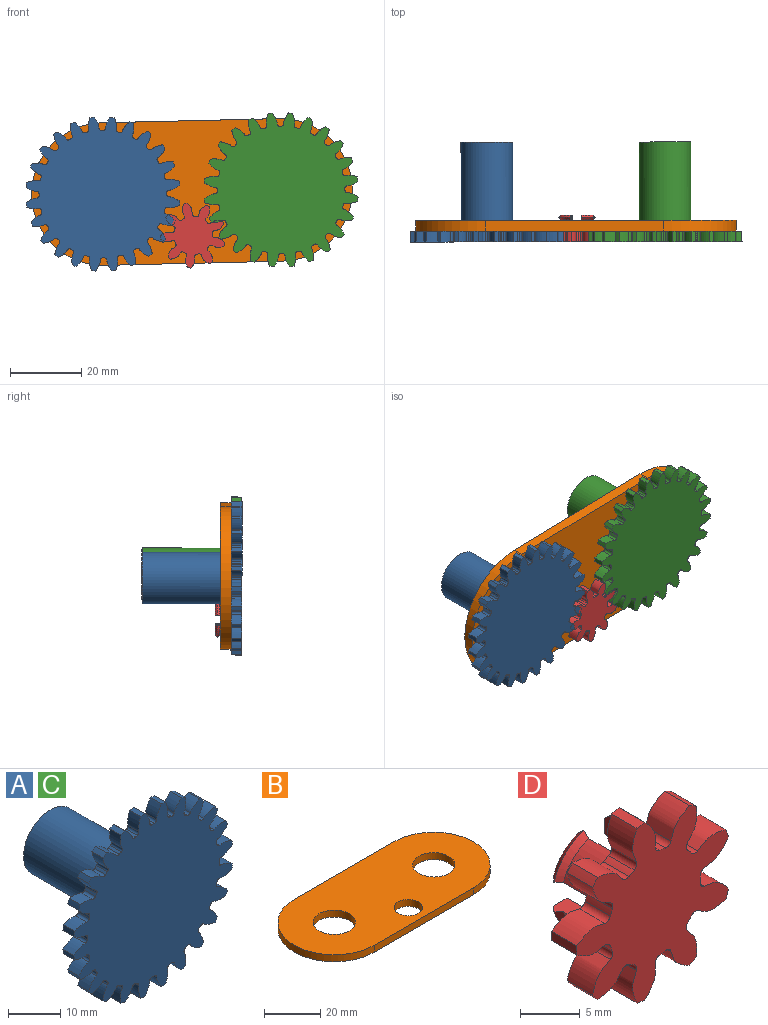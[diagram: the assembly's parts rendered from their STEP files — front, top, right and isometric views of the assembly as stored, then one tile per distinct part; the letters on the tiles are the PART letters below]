
ASSEMBLY  parts=4 mates=6
PART A: 148 faces, bbox 43.1x28x43.1 mm
  f0: extruded ~3.06x3mm, area 10.1mm2, adj f95,f96,f97,f98
  f1: cylinder r=17.92mm len=3mm, axis (0,1,0), area 1.9mm2, adj f96,f97,f98,f99
  f2: extruded ~3.06x3mm, area 10.1mm2, adj f3,f96,f97,f99
  f3: cylinder r=21.67mm len=3mm, axis (0,1,0), area 3.6mm2, adj f2,f4,f96,f97
  f4: extruded ~3.3x3mm, area 10.1mm2, adj f3,f96,f97,f100
  f5: cylinder r=17.92mm len=3mm, axis (0,1,0), area 1.9mm2, adj f96,f97,f100,f101
  f6: extruded ~3x2.62mm, area 10.1mm2, adj f7,f96,f97,f101
  f7: cylinder r=21.67mm len=3mm, axis (0,1,0), area 3.6mm2, adj f6,f8,f96,f97
  f8: extruded ~3.31x3mm, area 10.1mm2, adj f7,f96,f97,f102
  f9: cylinder r=17.92mm len=3mm, axis (0,1,0), area 1.9mm2, adj f96,f97,f102,f103
  f10: extruded ~3x2.66mm, area 10.1mm2, adj f11,f96,f97,f103
  f11: cylinder r=21.67mm len=3mm, axis (0,1,0), area 3.6mm2, adj f10,f12,f96,f97
  f12: extruded ~3.09x3mm, area 10.1mm2, adj f11,f96,f97,f104
  f13: cylinder r=17.92mm len=3mm, axis (0,1,0), area 1.9mm2, adj f96,f97,f104,f105
  f14: extruded ~3.09x3mm, area 10.1mm2, adj f15,f96,f97,f105
  f15: cylinder r=21.67mm len=3mm, axis (0,1,0), area 3.6mm2, adj f14,f16,f96,f97
  f16: extruded ~3x2.66mm, area 10.1mm2, adj f15,f96,f97,f106
  f17: cylinder r=17.92mm len=3mm, axis (0,1,0), area 1.9mm2, adj f96,f97,f106,f107
  f18: extruded ~3.31x3mm, area 10.1mm2, adj f19,f96,f97,f107
  f19: cylinder r=21.67mm len=3mm, axis (0,1,0), area 3.6mm2, adj f18,f20,f96,f97
  f20: extruded ~3x2.62mm, area 10.1mm2, adj f19,f96,f97,f108
  f21: cylinder r=17.92mm len=3mm, axis (0,1,0), area 1.9mm2, adj f96,f97,f108,f109
  f22: extruded ~3.3x3mm, area 10.1mm2, adj f23,f96,f97,f109
  f23: cylinder r=21.67mm len=3mm, axis (0,1,0), area 3.6mm2, adj f22,f24,f96,f97
  f24: extruded ~3.06x3mm, area 10.1mm2, adj f23,f96,f97,f110
  f25: cylinder r=17.92mm len=3mm, axis (0,1,0), area 1.9mm2, adj f96,f97,f110,f111
  f26: extruded ~3.06x3mm, area 10.1mm2, adj f27,f96,f97,f111
  f27: cylinder r=21.67mm len=3mm, axis (0,1,0), area 3.6mm2, adj f26,f28,f96,f97
  f28: extruded ~3.3x3mm, area 10.1mm2, adj f27,f96,f97,f112
  f29: cylinder r=17.92mm len=3mm, axis (0,1,0), area 1.9mm2, adj f96,f97,f112,f113
  f30: extruded ~3x2.62mm, area 10.1mm2, adj f31,f96,f97,f113
  f31: cylinder r=21.67mm len=3mm, axis (0,1,0), area 3.6mm2, adj f30,f32,f96,f97
  f32: extruded ~3.31x3mm, area 10.1mm2, adj f31,f96,f97,f114
  f33: cylinder r=17.92mm len=3mm, axis (0,1,0), area 1.9mm2, adj f96,f97,f114,f115
  f34: extruded ~3x2.66mm, area 10.1mm2, adj f35,f96,f97,f115
  f35: cylinder r=21.67mm len=3mm, axis (0,1,0), area 3.6mm2, adj f34,f36,f96,f97
  f36: extruded ~3.09x3mm, area 10.1mm2, adj f35,f96,f97,f116
  f37: cylinder r=17.92mm len=3mm, axis (0,1,0), area 1.9mm2, adj f96,f97,f116,f117
  f38: extruded ~3.09x3mm, area 10.1mm2, adj f39,f96,f97,f117
  f39: cylinder r=21.67mm len=3mm, axis (0,1,0), area 3.6mm2, adj f38,f40,f96,f97
  f40: extruded ~3x2.66mm, area 10.1mm2, adj f39,f96,f97,f118
  f41: cylinder r=17.92mm len=3mm, axis (0,1,0), area 1.9mm2, adj f96,f97,f118,f119
  f42: extruded ~3.31x3mm, area 10.1mm2, adj f43,f96,f97,f119
  f43: cylinder r=21.67mm len=3mm, axis (0,1,0), area 3.6mm2, adj f42,f44,f96,f97
  f44: extruded ~3x2.62mm, area 10.1mm2, adj f43,f96,f97,f120
  f45: cylinder r=17.92mm len=3mm, axis (0,1,0), area 1.9mm2, adj f96,f97,f120,f121
  f46: extruded ~3.3x3mm, area 10.1mm2, adj f47,f96,f97,f121
  f47: cylinder r=21.67mm len=3mm, axis (0,1,0), area 3.6mm2, adj f46,f48,f96,f97
  f48: extruded ~3.06x3mm, area 10.1mm2, adj f47,f96,f97,f122
  f49: cylinder r=17.92mm len=3mm, axis (0,1,0), area 1.9mm2, adj f96,f97,f122,f123
  f50: extruded ~3.06x3mm, area 10.1mm2, adj f51,f96,f97,f123
  f51: cylinder r=21.67mm len=3mm, axis (0,1,0), area 3.6mm2, adj f50,f52,f96,f97
  f52: extruded ~3.3x3mm, area 10.1mm2, adj f51,f96,f97,f124
  f53: cylinder r=17.92mm len=3mm, axis (0,1,0), area 1.9mm2, adj f96,f97,f124,f125
  f54: extruded ~3x2.62mm, area 10.1mm2, adj f55,f96,f97,f125
  f55: cylinder r=21.67mm len=3mm, axis (0,1,0), area 3.6mm2, adj f54,f56,f96,f97
  f56: extruded ~3.31x3mm, area 10.1mm2, adj f55,f96,f97,f126
  f57: cylinder r=17.92mm len=3mm, axis (0,1,0), area 1.9mm2, adj f96,f97,f126,f127
  f58: extruded ~3x2.66mm, area 10.1mm2, adj f59,f96,f97,f127
  f59: cylinder r=21.67mm len=3mm, axis (0,1,0), area 3.6mm2, adj f58,f60,f96,f97
  f60: extruded ~3.09x3mm, area 10.1mm2, adj f59,f96,f97,f128
  f61: cylinder r=17.92mm len=3mm, axis (0,1,0), area 1.9mm2, adj f96,f97,f128,f129
  f62: extruded ~3.09x3mm, area 10.1mm2, adj f63,f96,f97,f129
  f63: cylinder r=21.67mm len=3mm, axis (0,1,0), area 3.6mm2, adj f62,f64,f96,f97
  f64: extruded ~3x2.66mm, area 10.1mm2, adj f63,f96,f97,f130
  f65: cylinder r=17.92mm len=3mm, axis (0,1,0), area 1.9mm2, adj f96,f97,f130,f131
  f66: extruded ~3.31x3mm, area 10.1mm2, adj f67,f96,f97,f131
  f67: cylinder r=21.67mm len=3mm, axis (0,1,0), area 3.6mm2, adj f66,f68,f96,f97
  f68: extruded ~3x2.62mm, area 10.1mm2, adj f67,f96,f97,f132
  f69: cylinder r=17.92mm len=3mm, axis (0,1,0), area 1.9mm2, adj f96,f97,f132,f133
  f70: extruded ~3.3x3mm, area 10.1mm2, adj f71,f96,f97,f133
  f71: cylinder r=21.67mm len=3mm, axis (0,1,0), area 3.6mm2, adj f70,f72,f96,f97
  f72: extruded ~3.06x3mm, area 10.1mm2, adj f71,f96,f97,f134
  f73: cylinder r=17.92mm len=3mm, axis (0,1,0), area 1.9mm2, adj f96,f97,f134,f135
  f74: extruded ~3.06x3mm, area 10.1mm2, adj f75,f96,f97,f135
  f75: cylinder r=21.67mm len=3mm, axis (0,1,0), area 3.6mm2, adj f74,f76,f96,f97
  f76: extruded ~3.3x3mm, area 10.1mm2, adj f75,f96,f97,f136
  f77: cylinder r=17.92mm len=3mm, axis (0,1,0), area 1.9mm2, adj f96,f97,f136,f137
  f78: extruded ~3x2.62mm, area 10.1mm2, adj f79,f96,f97,f137
  f79: cylinder r=21.67mm len=3mm, axis (0,1,0), area 3.6mm2, adj f78,f80,f96,f97
  f80: extruded ~3.31x3mm, area 10.1mm2, adj f79,f96,f97,f138
  f81: cylinder r=17.92mm len=3mm, axis (0,1,0), area 1.9mm2, adj f96,f97,f138,f139
  f82: extruded ~3x2.66mm, area 10.1mm2, adj f83,f96,f97,f139
  f83: cylinder r=21.67mm len=3mm, axis (0,1,0), area 3.6mm2, adj f82,f84,f96,f97
  f84: extruded ~3.09x3mm, area 10.1mm2, adj f83,f96,f97,f140
  f85: cylinder r=17.92mm len=3mm, axis (0,1,0), area 1.9mm2, adj f96,f97,f140,f141
  f86: extruded ~3.09x3mm, area 10.1mm2, adj f87,f96,f97,f141
  f87: cylinder r=21.67mm len=3mm, axis (0,1,0), area 3.6mm2, adj f86,f88,f96,f97
  f88: extruded ~3x2.66mm, area 10.1mm2, adj f87,f96,f97,f142
  f89: cylinder r=17.92mm len=3mm, axis (0,1,0), area 1.9mm2, adj f96,f97,f142,f143
  f90: extruded ~3.31x3mm, area 10.1mm2, adj f91,f96,f97,f143
  f91: cylinder r=21.67mm len=3mm, axis (0,1,0), area 3.6mm2, adj f90,f92,f96,f97
  f92: extruded ~3x2.62mm, area 10.1mm2, adj f91,f96,f97,f144
  f93: cylinder r=17.92mm len=3mm, axis (0,1,0), area 1.9mm2, adj f96,f97,f144,f145
  f94: extruded ~3.3x3mm, area 10.1mm2, adj f95,f96,f97,f145
  f95: cylinder r=21.67mm len=3mm, axis (0,1,0), area 3.6mm2, adj f0,f94,f96,f97
  f96: plane 43.11x43.11mm, normal (0,-1,0), area 1236.6mm2, adj f0,f1,f2,f3,f4,f5,f6,f7
  f97: plane 43.11x43.11mm, normal (0,1,0), area 1071.4mm2, adj f0,f1,f2,f3,f4,f5,f6,f7
  f98: cylinder r=0.6mm len=3mm, axis (0,1,0), area 2.8mm2, adj f0,f1,f96,f97
  f99: cylinder r=0.6mm len=3mm, axis (0,1,0), area 2.8mm2, adj f1,f2,f96,f97
  f100: cylinder r=0.6mm len=3mm, axis (0,1,0), area 2.8mm2, adj f4,f5,f96,f97
  f101: cylinder r=0.6mm len=3mm, axis (0,1,0), area 2.8mm2, adj f5,f6,f96,f97
  f102: cylinder r=0.6mm len=3mm, axis (0,1,0), area 2.8mm2, adj f8,f9,f96,f97
  f103: cylinder r=0.6mm len=3mm, axis (0,1,0), area 2.8mm2, adj f9,f10,f96,f97
  f104: cylinder r=0.6mm len=3mm, axis (0,1,0), area 2.8mm2, adj f12,f13,f96,f97
  f105: cylinder r=0.6mm len=3mm, axis (0,1,0), area 2.8mm2, adj f13,f14,f96,f97
  f106: cylinder r=0.6mm len=3mm, axis (0,1,0), area 2.8mm2, adj f16,f17,f96,f97
  f107: cylinder r=0.6mm len=3mm, axis (0,1,0), area 2.8mm2, adj f17,f18,f96,f97
  f108: cylinder r=0.6mm len=3mm, axis (0,1,0), area 2.8mm2, adj f20,f21,f96,f97
  f109: cylinder r=0.6mm len=3mm, axis (0,1,0), area 2.8mm2, adj f21,f22,f96,f97
  f110: cylinder r=0.6mm len=3mm, axis (0,1,0), area 2.8mm2, adj f24,f25,f96,f97
  f111: cylinder r=0.6mm len=3mm, axis (0,1,0), area 2.8mm2, adj f25,f26,f96,f97
  f112: cylinder r=0.6mm len=3mm, axis (0,1,0), area 2.8mm2, adj f28,f29,f96,f97
  f113: cylinder r=0.6mm len=3mm, axis (0,1,0), area 2.8mm2, adj f29,f30,f96,f97
  f114: cylinder r=0.6mm len=3mm, axis (0,1,0), area 2.8mm2, adj f32,f33,f96,f97
  f115: cylinder r=0.6mm len=3mm, axis (0,1,0), area 2.8mm2, adj f33,f34,f96,f97
  f116: cylinder r=0.6mm len=3mm, axis (0,1,0), area 2.8mm2, adj f36,f37,f96,f97
  f117: cylinder r=0.6mm len=3mm, axis (0,1,0), area 2.8mm2, adj f37,f38,f96,f97
  f118: cylinder r=0.6mm len=3mm, axis (0,1,0), area 2.8mm2, adj f40,f41,f96,f97
  f119: cylinder r=0.6mm len=3mm, axis (0,1,0), area 2.8mm2, adj f41,f42,f96,f97
  f120: cylinder r=0.6mm len=3mm, axis (0,1,0), area 2.8mm2, adj f44,f45,f96,f97
  f121: cylinder r=0.6mm len=3mm, axis (0,1,0), area 2.8mm2, adj f45,f46,f96,f97
  f122: cylinder r=0.6mm len=3mm, axis (0,1,0), area 2.8mm2, adj f48,f49,f96,f97
  f123: cylinder r=0.6mm len=3mm, axis (0,1,0), area 2.8mm2, adj f49,f50,f96,f97
  f124: cylinder r=0.6mm len=3mm, axis (0,1,0), area 2.8mm2, adj f52,f53,f96,f97
  f125: cylinder r=0.6mm len=3mm, axis (0,1,0), area 2.8mm2, adj f53,f54,f96,f97
  f126: cylinder r=0.6mm len=3mm, axis (0,1,0), area 2.8mm2, adj f56,f57,f96,f97
  f127: cylinder r=0.6mm len=3mm, axis (0,1,0), area 2.8mm2, adj f57,f58,f96,f97
  f128: cylinder r=0.6mm len=3mm, axis (0,1,0), area 2.8mm2, adj f60,f61,f96,f97
  f129: cylinder r=0.6mm len=3mm, axis (0,1,0), area 2.8mm2, adj f61,f62,f96,f97
  f130: cylinder r=0.6mm len=3mm, axis (0,1,0), area 2.8mm2, adj f64,f65,f96,f97
  f131: cylinder r=0.6mm len=3mm, axis (0,1,0), area 2.8mm2, adj f65,f66,f96,f97
  f132: cylinder r=0.6mm len=3mm, axis (0,1,0), area 2.8mm2, adj f68,f69,f96,f97
  f133: cylinder r=0.6mm len=3mm, axis (0,1,0), area 2.8mm2, adj f69,f70,f96,f97
  f134: cylinder r=0.6mm len=3mm, axis (0,1,0), area 2.8mm2, adj f72,f73,f96,f97
  f135: cylinder r=0.6mm len=3mm, axis (0,1,0), area 2.8mm2, adj f73,f74,f96,f97
  f136: cylinder r=0.6mm len=3mm, axis (0,1,0), area 2.8mm2, adj f76,f77,f96,f97
  f137: cylinder r=0.6mm len=3mm, axis (0,1,0), area 2.8mm2, adj f77,f78,f96,f97
  f138: cylinder r=0.6mm len=3mm, axis (0,1,0), area 2.8mm2, adj f80,f81,f96,f97
  f139: cylinder r=0.6mm len=3mm, axis (0,1,0), area 2.8mm2, adj f81,f82,f96,f97
  f140: cylinder r=0.6mm len=3mm, axis (0,1,0), area 2.8mm2, adj f84,f85,f96,f97
  f141: cylinder r=0.6mm len=3mm, axis (0,1,0), area 2.8mm2, adj f85,f86,f96,f97
  f142: cylinder r=0.6mm len=3mm, axis (0,1,0), area 2.8mm2, adj f88,f89,f96,f97
  f143: cylinder r=0.6mm len=3mm, axis (0,1,0), area 2.8mm2, adj f89,f90,f96,f97
  f144: cylinder r=0.6mm len=3mm, axis (0,1,0), area 2.8mm2, adj f92,f93,f96,f97
  f145: cylinder r=0.6mm len=3mm, axis (0,1,0), area 2.8mm2, adj f93,f94,f96,f97
  f146: cylinder r=7.25mm len=25mm, axis (0,-1,0), area 1138.8mm2, adj f97,f147
  f147: plane 14.5x14.5mm, normal (0,1,0), area 165.1mm2, adj f146
PART B: 9 faces, bbox 90x40x3 mm
  f0: plane 50x3mm, normal (0,1,0), area 150mm2, adj f1,f5,f7,f8
  f1: cylinder r=20mm len=40mm, axis (0,0,-1), area 188.5mm2, adj f0,f2,f7,f8
  f2: plane 50x3mm, normal (0,-1,0), area 150mm2, adj f1,f5,f7,f8
  f3: cylinder r=5mm len=10mm, axis (0,0,-1), area 94.2mm2, adj f7,f8
  f4: cylinder r=7.5mm len=15mm, axis (0,0,-1), area 141.4mm2, adj f7,f8
  f5: cylinder r=20mm len=40mm, axis (0,0,-1), area 188.5mm2, adj f0,f2,f7,f8
  f6: cylinder r=7.5mm len=15mm, axis (0,0,-1), area 141.4mm2, adj f7,f8
  f7: plane 90x40mm, normal (0,0,1), area 2824.7mm2, adj f0,f1,f2,f3,f4,f5,f6
  f8: plane 90x40mm, normal (0,0,-1), area 2824.7mm2, adj f0,f1,f2,f3,f4,f5,f6
PART C: same geometry as A
PART D: 84 faces, bbox 18x7.4x18.3 mm
  f0: cylinder r=4.75mm len=3.25mm, axis (0,-1,0), area 14.3mm2, adj f6,f50,f72,f73
  f1: cylinder r=4.75mm len=3.25mm, axis (0,-1,0), area 14.3mm2, adj f7,f50,f76,f77
  f2: cylinder r=4.75mm len=3.25mm, axis (0,-1,0), area 14.3mm2, adj f8,f50,f78,f79
  f3: cone r=5.25mm half-angle=40deg, axis (0,-1,0), area 3.7mm2, adj f6,f9,f72,f73
  f4: cone r=5.25mm half-angle=40deg, axis (0,-1,0), area 3.7mm2, adj f7,f10,f76,f77
  f5: cone r=5.25mm half-angle=40deg, axis (0,-1,0), area 3.7mm2, adj f8,f11,f78,f79
  f6: cone r=4.75mm half-angle=40deg, axis (0,1,0), area 3.7mm2, adj f0,f3,f72,f73
  f7: cone r=4.75mm half-angle=40deg, axis (0,1,0), area 3.7mm2, adj f1,f4,f76,f77
  f8: cone r=4.75mm half-angle=40deg, axis (0,1,0), area 3.7mm2, adj f2,f5,f78,f79
  f9: plane 3.01x3.01mm, normal (0,1,0), area 4.8mm2, adj f3,f72,f73,f80
  f10: plane 3.01x3.01mm, normal (0,1,0), area 4.8mm2, adj f4,f76,f77,f82
  f11: plane 3.01x3.01mm, normal (0,1,0), area 4.8mm2, adj f5,f78,f79,f83
  f12: cylinder r=4.75mm len=3.25mm, axis (0,-1,0), area 14.3mm2, adj f50,f70,f74,f75
  f13: extruded ~3x2.88mm, area 10.5mm2, adj f48,f49,f50,f51
  f14: cylinder r=5.42mm len=3mm, axis (0,1,0), area 2.1mm2, adj f49,f50,f51,f52
  f15: extruded ~3x2.88mm, area 10.5mm2, adj f16,f49,f50,f52
  f16: cylinder r=9.17mm len=3mm, axis (0,1,0), area 2.8mm2, adj f15,f17,f49,f50
  f17: extruded ~3.32x3mm, area 10.5mm2, adj f16,f49,f50,f53
  f18: cylinder r=5.42mm len=3mm, axis (0,1,0), area 2.1mm2, adj f49,f50,f53,f54
  f19: extruded ~3.18x3mm, area 10.5mm2, adj f20,f49,f50,f54
  f20: cylinder r=9.17mm len=3mm, axis (0,1,0), area 2.8mm2, adj f19,f21,f49,f50
  f21: extruded ~3x2.53mm, area 10.5mm2, adj f20,f49,f50,f55
  f22: cylinder r=5.42mm len=3mm, axis (0,1,0), area 2.1mm2, adj f49,f50,f55,f56
  f23: extruded ~3.13x3mm, area 10.5mm2, adj f24,f49,f50,f56
  f24: cylinder r=9.17mm len=3mm, axis (0,1,0), area 2.8mm2, adj f23,f25,f49,f50
  f25: extruded ~3.36x3mm, area 10.5mm2, adj f24,f49,f50,f57
  f26: cylinder r=5.42mm len=3mm, axis (0,1,0), area 2.1mm2, adj f49,f50,f57,f58
  f27: extruded ~3x2.95mm, area 10.5mm2, adj f28,f49,f50,f58
  f28: cylinder r=9.17mm len=3mm, axis (0,1,0), area 2.8mm2, adj f27,f29,f49,f50
  f29: extruded ~3x2.62mm, area 10.5mm2, adj f28,f49,f50,f59
  f30: cylinder r=5.42mm len=3mm, axis (0,1,0), area 2.1mm2, adj f49,f50,f59,f60
  f31: extruded ~3.3x3mm, area 10.5mm2, adj f32,f49,f50,f60
  f32: cylinder r=9.17mm len=3mm, axis (0,1,0), area 2.8mm2, adj f31,f33,f49,f50
  f33: extruded ~3.3x3mm, area 10.5mm2, adj f32,f49,f50,f61
  f34: cylinder r=5.42mm len=3mm, axis (0,1,0), area 2.1mm2, adj f49,f50,f61,f62
  f35: extruded ~3x2.62mm, area 10.5mm2, adj f36,f49,f50,f62
  f36: cylinder r=9.17mm len=3mm, axis (0,1,0), area 2.8mm2, adj f35,f37,f49,f50
  f37: extruded ~3x2.95mm, area 10.5mm2, adj f36,f49,f50,f63
  f38: cylinder r=5.42mm len=3mm, axis (0,1,0), area 2.1mm2, adj f49,f50,f63,f64
  f39: extruded ~3.36x3mm, area 10.5mm2, adj f40,f49,f50,f64
  f40: cylinder r=9.17mm len=3mm, axis (0,1,0), area 2.8mm2, adj f39,f41,f49,f50
  f41: extruded ~3.13x3mm, area 10.5mm2, adj f40,f49,f50,f65
  f42: cylinder r=5.42mm len=3mm, axis (0,1,0), area 2.1mm2, adj f49,f50,f65,f66
  f43: extruded ~3x2.53mm, area 10.5mm2, adj f44,f49,f50,f66
  f44: cylinder r=9.17mm len=3mm, axis (0,1,0), area 2.8mm2, adj f43,f45,f49,f50
  f45: extruded ~3.18x3mm, area 10.5mm2, adj f44,f49,f50,f67
  f46: cylinder r=5.42mm len=3mm, axis (0,1,0), area 2.1mm2, adj f49,f50,f67,f68
  f47: extruded ~3.32x3mm, area 10.5mm2, adj f48,f49,f50,f68
  f48: cylinder r=9.17mm len=3mm, axis (0,1,0), area 2.8mm2, adj f13,f47,f49,f50
  f49: plane 18.28x18mm, normal (0,-1,0), area 168mm2, adj f13,f14,f15,f16,f17,f18,f19,f20
  f50: plane 18.28x18mm, normal (0,1,0), area 148.7mm2, adj f0,f1,f2,f12,f13,f14,f15,f16
  f51: cylinder r=0.57mm len=3mm, axis (0,1,0), area 2.5mm2, adj f13,f14,f49,f50
  f52: cylinder r=0.57mm len=3mm, axis (0,1,0), area 2.5mm2, adj f14,f15,f49,f50
  f53: cylinder r=0.57mm len=3mm, axis (0,1,0), area 2.5mm2, adj f17,f18,f49,f50
  f54: cylinder r=0.57mm len=3mm, axis (0,1,0), area 2.5mm2, adj f18,f19,f49,f50
  f55: cylinder r=0.57mm len=3mm, axis (0,1,0), area 2.5mm2, adj f21,f22,f49,f50
  f56: cylinder r=0.57mm len=3mm, axis (0,1,0), area 2.5mm2, adj f22,f23,f49,f50
  f57: cylinder r=0.57mm len=3mm, axis (0,1,0), area 2.5mm2, adj f25,f26,f49,f50
  f58: cylinder r=0.57mm len=3mm, axis (0,1,0), area 2.5mm2, adj f26,f27,f49,f50
  f59: cylinder r=0.57mm len=3mm, axis (0,1,0), area 2.5mm2, adj f29,f30,f49,f50
  f60: cylinder r=0.57mm len=3mm, axis (0,1,0), area 2.5mm2, adj f30,f31,f49,f50
  f61: cylinder r=0.57mm len=3mm, axis (0,1,0), area 2.5mm2, adj f33,f34,f49,f50
  f62: cylinder r=0.57mm len=3mm, axis (0,1,0), area 2.5mm2, adj f34,f35,f49,f50
  f63: cylinder r=0.57mm len=3mm, axis (0,1,0), area 2.5mm2, adj f37,f38,f49,f50
  f64: cylinder r=0.57mm len=3mm, axis (0,1,0), area 2.5mm2, adj f38,f39,f49,f50
  f65: cylinder r=0.57mm len=3mm, axis (0,1,0), area 2.5mm2, adj f41,f42,f49,f50
  f66: cylinder r=0.57mm len=3mm, axis (0,1,0), area 2.5mm2, adj f42,f43,f49,f50
  f67: cylinder r=0.57mm len=3mm, axis (0,1,0), area 2.5mm2, adj f45,f46,f49,f50
  f68: cylinder r=0.57mm len=3mm, axis (0,1,0), area 2.5mm2, adj f46,f47,f49,f50
  f69: cone r=5.25mm half-angle=40deg, axis (0,-1,0), area 3.7mm2, adj f70,f71,f74,f75
  f70: cone r=4.75mm half-angle=40deg, axis (0,1,0), area 3.7mm2, adj f12,f69,f74,f75
  f71: plane 3.01x3.01mm, normal (0,1,0), area 4.8mm2, adj f69,f74,f75,f81
  f72: plane 4.45x2.16mm, normal (-1,0,0), area 7.5mm2, adj f0,f3,f6,f9,f50,f80
  f73: plane 4.45x2.16mm, normal (0,0,-1), area 7.5mm2, adj f0,f3,f6,f9,f50,f80
  f74: plane 4.45x2.16mm, normal (0,0,1), area 7.5mm2, adj f12,f50,f69,f70,f71,f81
  f75: plane 4.45x2.16mm, normal (-1,0,0), area 7.5mm2, adj f12,f50,f69,f70,f71,f81
  f76: plane 4.45x2.16mm, normal (1,0,0), area 7.5mm2, adj f1,f4,f7,f10,f50,f82
  f77: plane 4.45x2.16mm, normal (0,0,1), area 7.5mm2, adj f1,f4,f7,f10,f50,f82
  f78: plane 4.45x2.16mm, normal (0,0,-1), area 7.5mm2, adj f2,f5,f8,f11,f50,f83
  f79: plane 4.45x2.16mm, normal (1,0,0), area 7.5mm2, adj f2,f5,f8,f11,f50,f83
  f80: cylinder r=3.25mm len=4.44mm, axis (0,1,0), area 8.8mm2, adj f9,f50,f72,f73
  f81: cylinder r=3.25mm len=4.44mm, axis (0,1,0), area 8.8mm2, adj f50,f71,f74,f75
  f82: cylinder r=3.25mm len=4.44mm, axis (0,1,0), area 8.8mm2, adj f10,f50,f76,f77
  f83: cylinder r=3.25mm len=4.44mm, axis (0,1,0), area 8.8mm2, adj f11,f50,f78,f79
PLACE A rot(axis=(0,1,0),44.4deg) t=(34.67,25.49,-63.24)mm
PLACE B rot(axis=(1,-0.01,0.01),90.1deg) t=(34.67,28.49,-63.23)mm
PLACE C rot(axis=(0,1,0),44.4deg) t=(84.66,25.53,-62.06)mm
PLACE D rot(axis=(0.03,-1,0.01),3.4deg) t=(59.95,25.53,-74.83)mm
MATE planar C.f97 <-> B.f7  axis (0,1,0) through (102.58,25.56,-70.71)mm
MATE cylindrical A.f3 <-> B.f1  axis (0,1,0) through (34.65,50.49,-63.19)mm
MATE planar B.f7 <-> D.f14  axis (0,-1,0) through (59.66,25.51,-62.31)mm
MATE planar A.f97 <-> B.f7  axis (0,1,0) through (43.27,25.52,-79.63)mm
MATE cylindrical D.f0 <-> B.f3  axis (0,-1,0) through (59.95,22.53,-74.84)mm
MATE cylindrical B.f5 <-> C.f3  axis (0,-1,0) through (84.66,25.53,-62.06)mm
